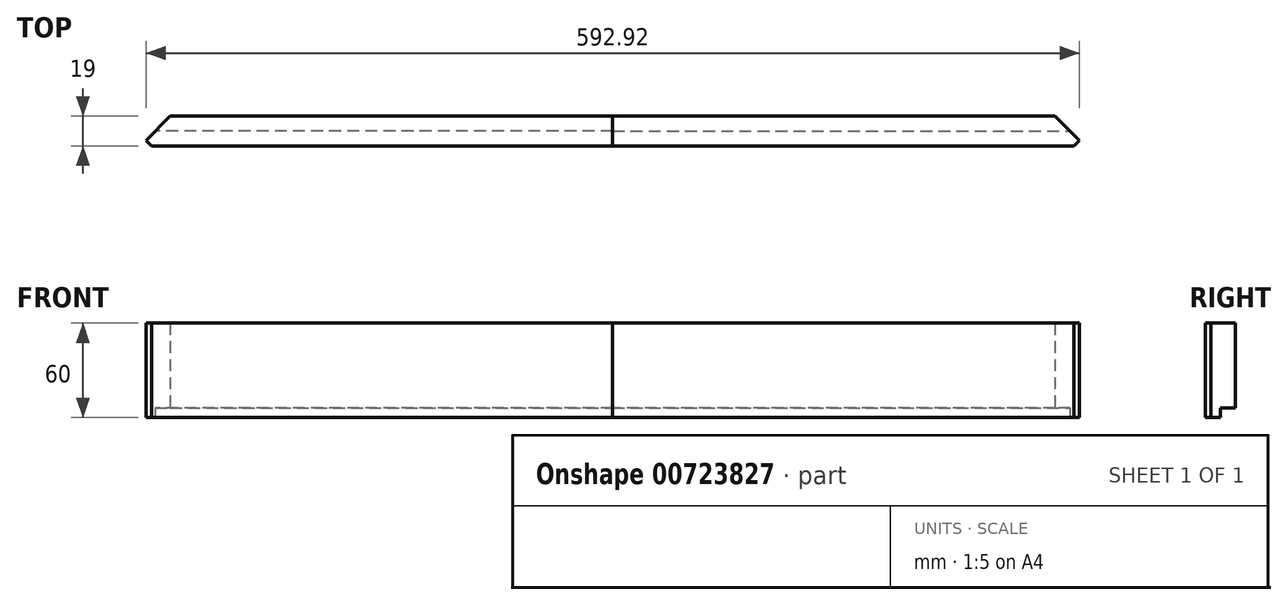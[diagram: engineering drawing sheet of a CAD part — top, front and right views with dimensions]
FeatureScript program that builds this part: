
annotation { "Feature Type Name" : "Feature", "Feature Type Description" : "" }
export const myFeature = defineFeature(function(context is Context, id is Id, definition is map)
    precondition{}
    {
        {
            var Q0;
            Q0=qCreatedBy(makeId("Top.planeOp"),FACE);
            var sketch = newSketch(context, id + "F0", { "sketchPlane" : qUnion([Q0])});
            skLineSegment(sketch, "E0", {"start": v(0, 0) * mm, "end": v(292.93, 0) * mm});
            skLineSegment(sketch, "E1", {"start": v(292.93, 0) * mm, "end": v(296.46, 3.54) * mm});
            skLineSegment(sketch, "E2", {"start": v(296.46, 3.54) * mm, "end": v(281, 19) * mm});
            skLineSegment(sketch, "E3", {"start": v(281, 19) * mm, "end": v(0, 19) * mm});
            skLineSegment(sketch, "E4", {"start": v(0, 19) * mm, "end": v(0, 0) * mm});
            skLineSegment(sketch, "E5", {"start": v(0, 9.5) * mm, "end": v(290.5, 9.5) * mm});
            skSolve(sketch);
        }
        {
            var Q0;
            Q0=makeQuery(id+"F0.imprint","IMPRINT",FACE,{"disambiguationData":[TD([[makeQuery(id+"F0.imprint","IMPRINT",EDGE,{"derivedFrom":sQuery(id+"F0.wireOp",EDGE,"E0")}),1.0]])]});
            var Q1;
            {var subQ0=sQuery(id+"F0.wireOp",EDGE,"E3");Q1=makeQuery(id+"F0.imprint","IMPRINT",FACE,{"disambiguationData":[TD([[makeQuery(id+"F0.imprint","IMPRINT",EDGE,{"derivedFrom":subQ0}),1.0]])]});}
            extrude(context, id + "F1", {"entities" : qUnion([Q0, Q1]), "depth" : 60 * mm, "offsetDistance" : 25 * mm});
        }
        {
            var Q0;
            {var subQ0=sQuery(id+"F0.wireOp",EDGE,"E3");Q0=makeQuery(id+"F0.imprint","IMPRINT",FACE,{"disambiguationData":[TD([[makeQuery(id+"F0.imprint","IMPRINT",EDGE,{"derivedFrom":subQ0}),1.0]])]});}
            extrude(context, id + "F2", {"entities" : qUnion([Q0]), "operationType" : NewBodyOperationType.REMOVE, "oppositeDirection" : true, "depth" : -6 * mm, "offsetDistance" : 25 * mm});
        }
        {
            var Q0;
            Q0=makeQuery(id+"F1.opExtrude","SWEPT_BODY",BODY,{"disambiguationData":[OSD([sQuery(id+"F0.wireOp",EDGE,"E0"),sQuery(id+"F0.wireOp",EDGE,"E1"),sQuery(id+"F0.wireOp",EDGE,"E2"),sQuery(id+"F0.wireOp",EDGE,"E3"),sQuery(id+"F0.wireOp",EDGE,"E4")])]});
            var Q1;
            Q1=qCreatedBy(makeId("Right.planeOp"),FACE);
            mirror(context, id + "F3", {"entities" : qUnion([Q0]), "mirrorPlane" : qUnion([Q1])});
        }
    });
